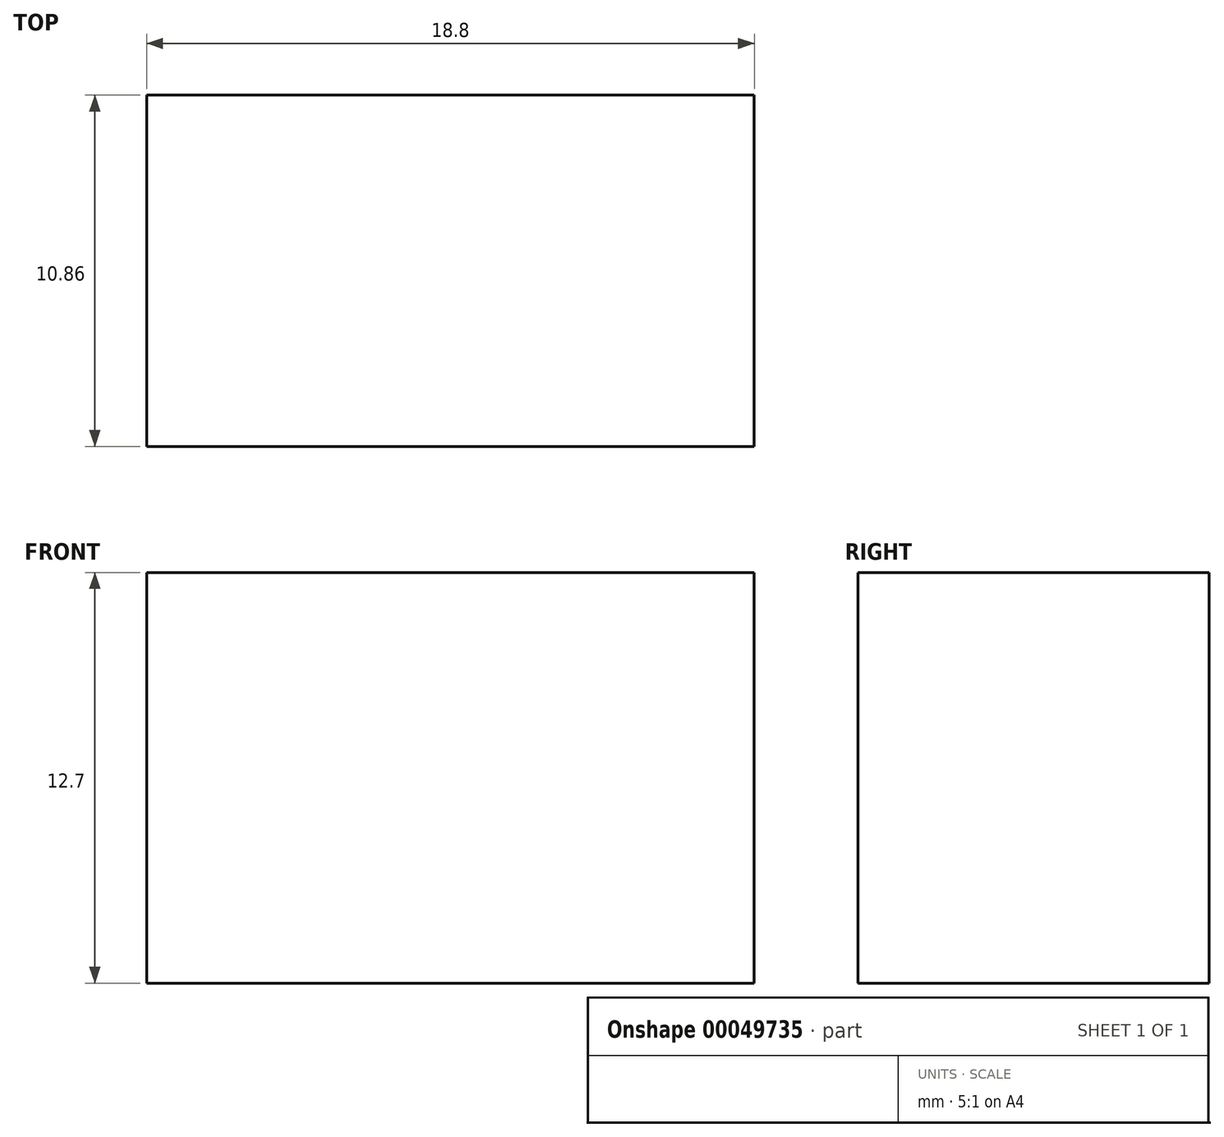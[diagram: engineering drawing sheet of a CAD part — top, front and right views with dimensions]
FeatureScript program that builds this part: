
annotation { "Feature Type Name" : "Feature", "Feature Type Description" : "" }
export const myFeature = defineFeature(function(context is Context, id is Id, definition is map)
    precondition{}
    {
        {
            var Q0;
            Q0=qCreatedBy(makeId("Top.planeOp"),FACE);
            var sketch = newSketch(context, id + "F0", { "sketchPlane" : qUnion([Q0])});
            skLineSegment(sketch, "E0.rect.bottom", {"start": v(-9.4, 5.43) * mm, "end": v(9.4, 5.43) * mm});
            skLineSegment(sketch, "E0.rect.top", {"start": v(-9.4, -5.43) * mm, "end": v(9.4, -5.43) * mm});
            skLineSegment(sketch, "E0.rect.left", {"start": v(-9.4, 5.43) * mm, "end": v(-9.4, -5.43) * mm});
            skLineSegment(sketch, "E0.rect.right", {"start": v(9.4, 5.43) * mm, "end": v(9.4, -5.43) * mm});
            skPoint(sketch, "E0.rect.middle", {"position": v(0, 0) * mm});
            skSolve(sketch);
        }
        {
            var Q0;
            Q0=makeQuery(id+"F0.imprint","IMPRINT",FACE,{"disambiguationData":[TD([[makeQuery(id+"F0.imprint","IMPRINT",EDGE,{"derivedFrom":sQuery(id+"F0.wireOp",EDGE,"E0.rect.bottom")}),-1.0]])]});
            extrude(context, id + "F1", {"entities" : qUnion([Q0]), "depth" : 12.7 * mm, "symmetric" : true});
        }
    });
